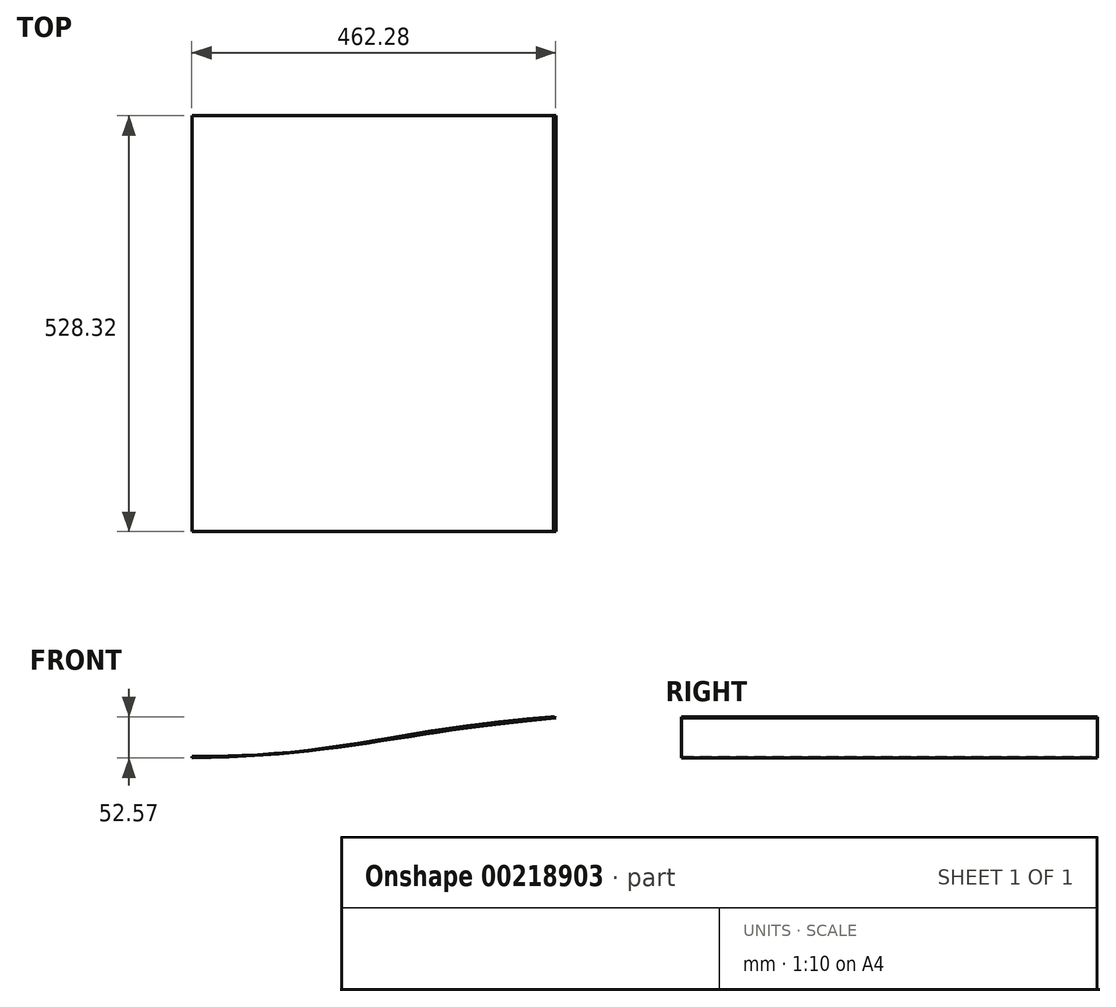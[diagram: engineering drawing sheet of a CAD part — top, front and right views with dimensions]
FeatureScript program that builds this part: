
annotation { "Feature Type Name" : "Feature", "Feature Type Description" : "" }
export const myFeature = defineFeature(function(context is Context, id is Id, definition is map)
    precondition{}
    {
        {
            var Q0;
            Q0=qCreatedBy(makeId("Front.planeOp"),FACE);
            var sketch = newSketch(context, id + "F0", { "sketchPlane" : qUnion([Q0])});
            skLineSegment(sketch, "E0", {"start": v(-209.55, -84.57) * mm, "end": v(-209.55, 27.19) * mm});
            skLineSegment(sketch, "E1", {"start": v(-209.55, 27.19) * mm, "end": v(-44.52, 99.91) * mm});
            skLineSegment(sketch, "E2", {"start": v(-44.52, 99.91) * mm, "end": v(36.76, 99.91) * mm});
            skLineSegment(sketch, "E3", {"start": v(36.76, 99.91) * mm, "end": v(252.73, -33.77) * mm});
            skLineSegment(sketch, "E4", {"start": v(-209.55, -84.57) * mm, "end": v(354.22, -84.57) * mm, "construction": true});
            skLineSegment(sketch, "E5", {"start": v(252.73, -33.77) * mm, "end": v(214.92, -33.77) * mm, "construction": true});
            skFitSpline(sketch, "E6", {"points": [v(-209.55, -84.57) * mm, v(252.73, -33.77) * mm], "startDerivative": vector(569.77, 9.08) * mm, "endDerivative": vector(578.08, 50.6) * mm});
            skLineSegment(sketch, "E7.0", {"start": v(36.2, 97.91) * mm, "end": v(246.57, -32.31) * mm});
            skLineSegment(sketch, "E7.1", {"start": v(-44.1, 97.91) * mm, "end": v(36.2, 97.91) * mm});
            skFitSpline(sketch, "E7.2", {"points": [v(-209.58, -82.57) * mm, v(-162.15, -81.82) * mm, v(-81.09, -76.83) * mm, v(20.15, -62.82) * mm, v(122.05, -46.2) * mm, v(204.35, -36) * mm, v(252.56, -31.78) * mm]});
            skLineSegment(sketch, "E7.3", {"start": v(-207.55, -82.54) * mm, "end": v(-207.55, 25.88) * mm});
            skLineSegment(sketch, "E7.4", {"start": v(-207.55, 25.88) * mm, "end": v(-44.1, 97.91) * mm});
            skSolve(sketch);
        }
        {
            var Q0;
            Q0=makeQuery(id+"F0.imprint","IMPRINT",FACE,{"disambiguationData":[TD([[makeQuery(id+"F0.imprint","IMPRINT",EDGE,{"derivedFrom":sQuery(id+"F0.wireOp",EDGE,"E0")}),-1.0]])]});
            extrude(context, id + "F1", {"entities" : qUnion([Q0]), "depth" : 528.32 * mm});
        }
    });
